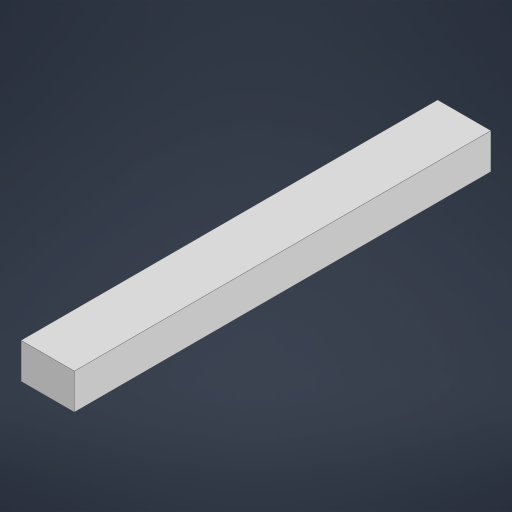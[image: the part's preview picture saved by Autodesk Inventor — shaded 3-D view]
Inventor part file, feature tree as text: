
AUTODESK INVENTOR PART (.ipt)
format: ipt  version: 2024 (Build 280153000, 153)  size: 190,464 bytes
history: native  units: mm
features: extrude x1, sketch x1
ambient origin geometry x8: Origin, YZ Plane, XZ Plane, XY Plane, X Axis, Y Axis, Z Axis, Center Point
bodies: Solid1 (feature_tree)
feature tree (2):
  extrude  "Extrusion1"  Depth=234.5mm
  sketch  "Sketch1"  dims[d0=30.0mm d1=234.5mm d2=20.0mm d3=0.0mm]
